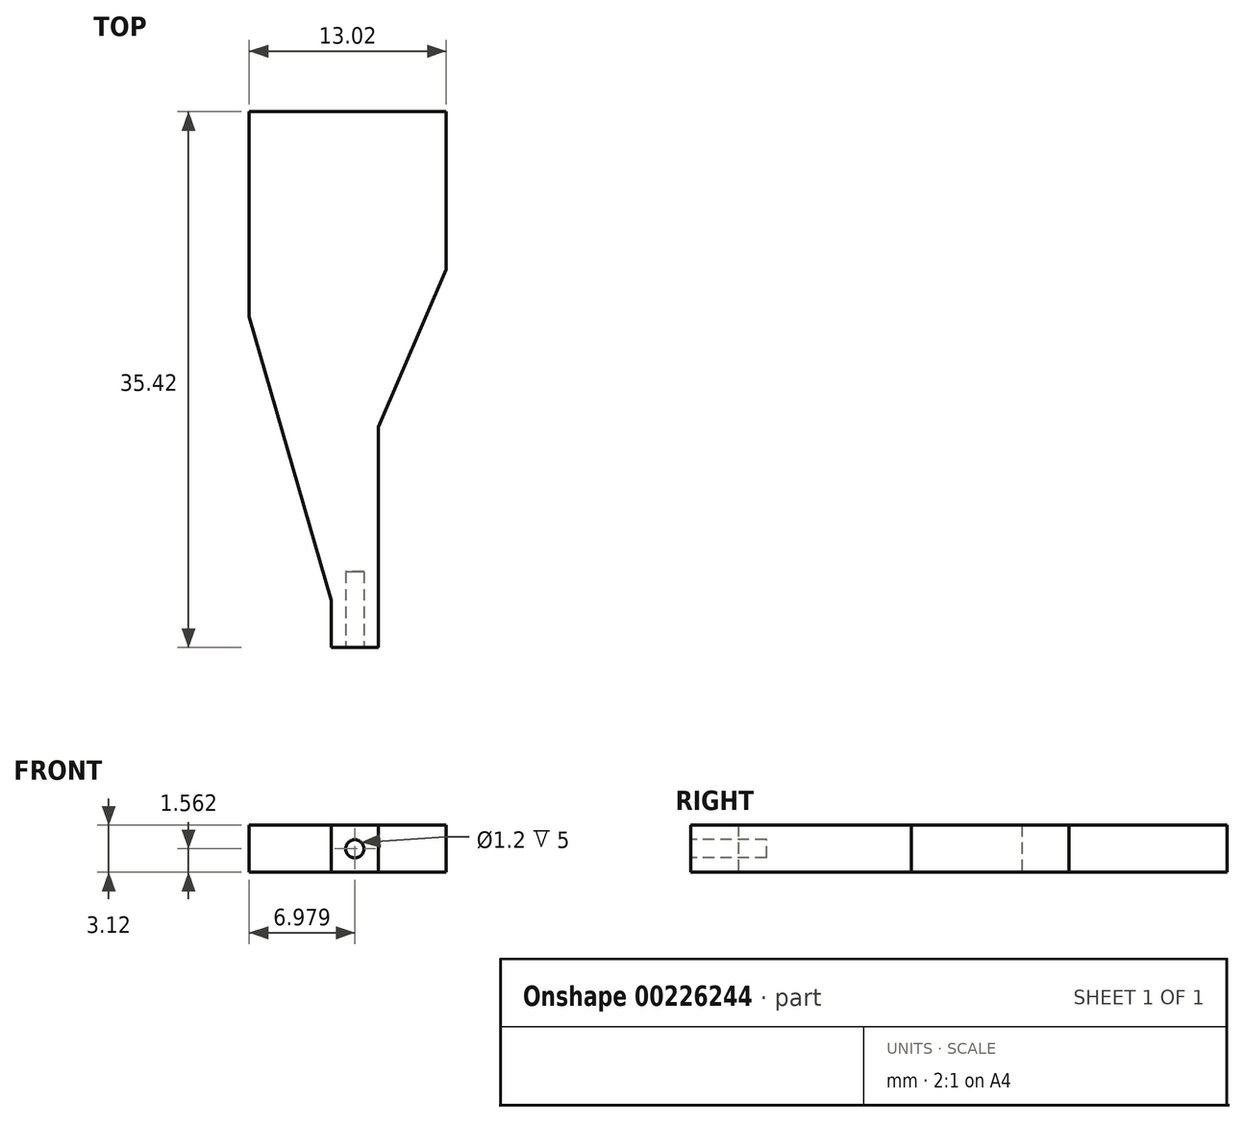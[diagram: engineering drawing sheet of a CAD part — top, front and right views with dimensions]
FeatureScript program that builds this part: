
annotation { "Feature Type Name" : "Feature", "Feature Type Description" : "" }
export const myFeature = defineFeature(function(context is Context, id is Id, definition is map)
    precondition{}
    {
        {
            var Q0;
            Q0=qCreatedBy(makeId("Top.planeOp"),FACE);
            var sketch = newSketch(context, id + "F0", { "sketchPlane" : qUnion([Q0])});
            skLineSegment(sketch, "E0", {"start": v(0, 0) * mm, "end": v(13.02, 0) * mm});
            skLineSegment(sketch, "E1", {"start": v(13.02, 0) * mm, "end": v(13.02, -10.42) * mm});
            skLineSegment(sketch, "E2", {"start": v(13.02, -10.42) * mm, "end": v(8.54, -20.83) * mm});
            skLineSegment(sketch, "E3", {"start": v(8.54, -20.83) * mm, "end": v(8.54, -35.42) * mm});
            skLineSegment(sketch, "E4", {"start": v(8.54, -35.42) * mm, "end": v(5.42, -35.42) * mm});
            skLineSegment(sketch, "E5", {"start": v(5.42, -35.42) * mm, "end": v(5.42, -32.3) * mm});
            skLineSegment(sketch, "E6", {"start": v(5.42, -32.3) * mm, "end": v(0, -13.54) * mm});
            skLineSegment(sketch, "E7", {"start": v(0, -13.54) * mm, "end": v(0, 0) * mm});
            skLineSegment(sketch, "E8", {"start": v(0, -13.13) * mm, "end": v(13.02, -13.13) * mm, "construction": true});
            skLineSegment(sketch, "E9", {"start": v(13.02, -13.12) * mm, "end": v(13.02, -10.42) * mm, "construction": true});
            skLineSegment(sketch, "E10", {"start": v(6.98, 0) * mm, "end": v(6.98, -35.42) * mm, "construction": true});
            skLineSegment(sketch, "E11", {"start": v(13.02, 0) * mm, "end": v(33.85, 0) * mm, "construction": true});
            skLineSegment(sketch, "E12", {"start": v(14.58, 0) * mm, "end": v(14.58, -35.42) * mm, "construction": true});
            skPoint(sketch, "E13", {"position": v(23.44, 0) * mm});
            skCircle(sketch, "E14", {"center": v(8.02, -8.33) * mm, "radius": 3.85 * mm, "construction": true});
            skSolve(sketch);
        }
        {
            var Q0;
            Q0 = qSketchRegion(id + "F0", true);
            extrude(context, id + "F1", {"entities" : qUnion([Q0]), "depth" : (150 / 48) * mm});
        }
        {
            var Q0;
            Q0=makeQuery(id+"F1.opExtrude","SWEPT_FACE",FACE,{"disambiguationData":[OSD([sQuery(id+"F0.wireOp",EDGE,"E4")])]});
            var sketch = newSketch(context, id + "F2", { "sketchPlane" : qUnion([Q0])});
            skLineSegment(sketch, "E15", {"start": v(5.42, 0) * mm, "end": v(8.54, 3.12) * mm, "construction": true});
            skPoint(sketch, "E16", {"position": v(6.98, 1.56) * mm});
            skCircle(sketch, "E17", {"center": v(6.98, 1.56) * mm, "radius": 0.6 * mm});
            skSolve(sketch);
        }
        {
            var Q0;
            Q0=makeQuery(id+"F2.imprint","IMPRINT",FACE,{"disambiguationData":[TD([[makeQuery(id+"F2.imprint","IMPRINT",EDGE,{"derivedFrom":sQuery(id+"F2.wireOp",EDGE,"E17")}),1.0]])]});
            extrude(context, id + "F3", {"entities" : qUnion([Q0]), "operationType" : NewBodyOperationType.REMOVE, "oppositeDirection" : true, "depth" : 5 * mm});
        }
    });
